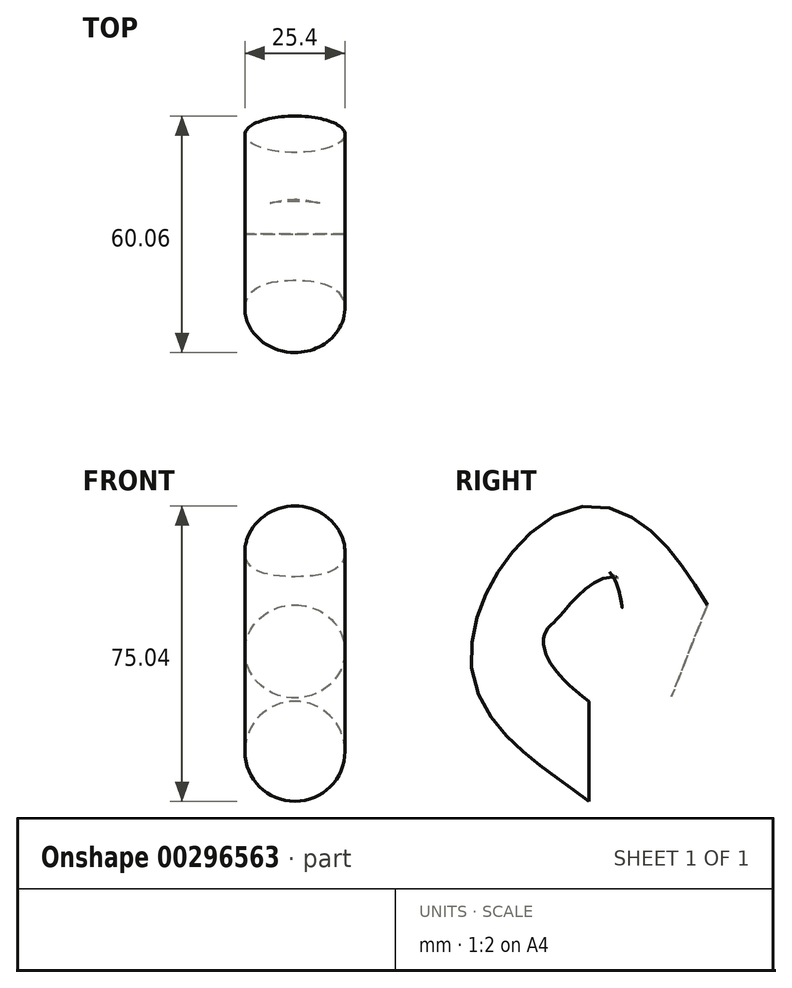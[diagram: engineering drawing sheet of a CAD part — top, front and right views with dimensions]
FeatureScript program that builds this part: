
annotation { "Feature Type Name" : "Feature", "Feature Type Description" : "" }
export const myFeature = defineFeature(function(context is Context, id is Id, definition is map)
    precondition{}
    {
        {
            var Q0;
            Q0=qCreatedBy(makeId("Front.planeOp"),FACE);
            var sketch = newSketch(context, id + "F0", { "sketchPlane" : qUnion([Q0])});
            skCircle(sketch, "E0", {"center": v(0, 0) * mm, "radius": 12.7 * mm});
            skSolve(sketch);
        }
        {
            var Q0;
            Q0=qCreatedBy(makeId("Right.planeOp"),FACE);
            var sketch = newSketch(context, id + "F1", { "sketchPlane" : qUnion([Q0])});
            skCircle(sketch, "E1", {"center": v(0, 25.4) * mm, "radius": 25.4 * mm});
            skCircle(sketch, "E2", {"center": v(0, -25.4) * mm, "radius": 25.4 * mm});
            skLineSegment(sketch, "E3", {"start": v(19.05, -71.01) * mm, "end": v(19.05, 67.26) * mm});
            skLineSegment(sketch, "E4.MirrorCS", {"start": v(-19.05, -71.01) * mm, "end": v(-19.05, 67.26) * mm});
            skFitSpline(sketch, "E5", {"points": [v(0, 0) * mm, v(-19.05, 25.4) * mm, v(0, 50.8) * mm, v(25.4, 25.4) * mm], "startDerivative": vector(-88.47, 68.08) * mm, "endDerivative": vector(69.21, -114.58) * mm});
            skFitSpline(sketch, "E6", {"points": [v(0, 0) * mm, v(19.05, -25.4) * mm, v(0, -50.8) * mm, v(-25.4, -25.4) * mm], "startDerivative": vector(88.47, -68.08) * mm, "endDerivative": vector(-69.21, 114.58) * mm});
            skSolve(sketch);
        }
        {
            var Q0;
            Q0=makeQuery(id+"F0.imprint","IMPRINT",FACE,{"disambiguationData":[TD([[makeQuery(id+"F0.imprint","IMPRINT",EDGE,{"derivedFrom":sQuery(id+"F0.wireOp",EDGE,"E0")}),1.0]])]});
            var Q1;
            Q1=sQuery(id+"F1.wireOp",EDGE,"E5");
            sweep(context, id + "F2", {"profiles" : qUnion([Q0]), "path" : qUnion([Q1])});
        }
    });
